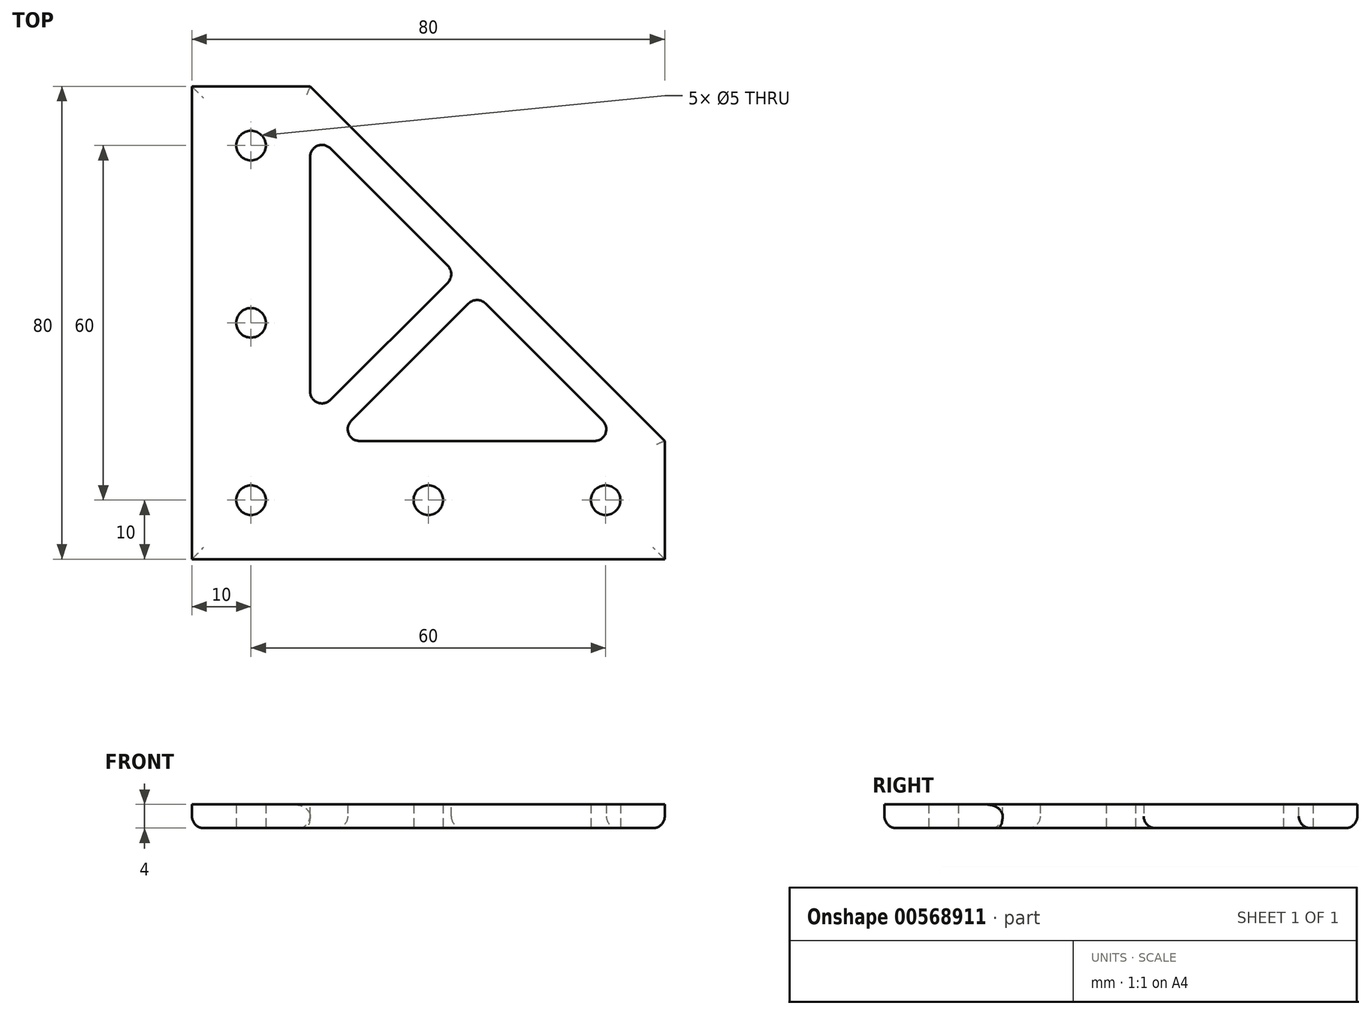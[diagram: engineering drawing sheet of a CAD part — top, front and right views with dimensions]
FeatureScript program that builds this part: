
annotation { "Feature Type Name" : "Feature", "Feature Type Description" : "" }
export const myFeature = defineFeature(function(context is Context, id is Id, definition is map)
    precondition{}
    {
        {
            var Q0;
            Q0=qCreatedBy(makeId("Top.planeOp"),FACE);
            var sketch = newSketch(context, id + "F0", { "sketchPlane" : qUnion([Q0])});
            skLineSegment(sketch, "E0", {"start": v(0, 0) * mm, "end": v(0, 80) * mm});
            skLineSegment(sketch, "E1", {"start": v(0, 80) * mm, "end": v(20, 80) * mm});
            skLineSegment(sketch, "E2", {"start": v(20, 80) * mm, "end": v(80, 20) * mm});
            skLineSegment(sketch, "E3", {"start": v(80, 20) * mm, "end": v(80, 0) * mm});
            skLineSegment(sketch, "E4", {"start": v(80, 0) * mm, "end": v(0, 0) * mm});
            skLineSegment(sketch, "E5", {"start": v(10, 80) * mm, "end": v(10, 0) * mm, "construction": true});
            skLineSegment(sketch, "E6", {"start": v(80, 10) * mm, "end": v(0, 10) * mm, "construction": true});
            skCircle(sketch, "E7", {"center": v(10, 70) * mm, "radius": 2.5 * mm});
            skCircle(sketch, "E8", {"center": v(10, 40) * mm, "radius": 2.5 * mm});
            skCircle(sketch, "E9", {"center": v(40, 10) * mm, "radius": 2.5 * mm});
            skCircle(sketch, "E10", {"center": v(70, 10) * mm, "radius": 2.5 * mm});
            skCircle(sketch, "E11", {"center": v(10, 10) * mm, "radius": 2.5 * mm});
            skSolve(sketch);
        }
        {
            var Q0;
            Q0=makeQuery(id+"F0.imprint","IMPRINT",FACE,{"disambiguationData":[TD([[makeQuery(id+"F0.imprint","IMPRINT",EDGE,{"derivedFrom":sQuery(id+"F0.wireOp",EDGE,"E0")}),-1.0]])]});
            extrude(context, id + "F1", {"entities" : qUnion([Q0]), "depth" : 4 * mm, "offsetDistance" : 25 * mm});
        }
        {
            var Q0;
            Q0=makeQuery(id+"F1.opExtrude","CAP_FACE",FACE,{"disambiguationData":[OSD([sQuery(id+"F0.wireOp",EDGE,"E0"),sQuery(id+"F0.wireOp",EDGE,"E1"),sQuery(id+"F0.wireOp",EDGE,"E2"),sQuery(id+"F0.wireOp",EDGE,"E3"),sQuery(id+"F0.wireOp",EDGE,"E4"),sQuery(id+"F0.wireOp",EDGE,"E7"),sQuery(id+"F0.wireOp",EDGE,"E8"),sQuery(id+"F0.wireOp",EDGE,"E9"),sQuery(id+"F0.wireOp",EDGE,"E10")])],"isStart":false});
            var sketch = newSketch(context, id + "F2", { "sketchPlane" : qUnion([Q0])});
            skLineSegment(sketch, "E12.0", {"start": v(20, 80) * mm, "end": v(80, 20) * mm, "construction": true});
            skLineSegment(sketch, "E13", {"start": v(20, 72.93) * mm, "end": v(20, 23.54) * mm});
            skLineSegment(sketch, "E14", {"start": v(72.93, 20) * mm, "end": v(23.54, 20) * mm});
            skPoint(sketch, "E15.orphan", {"position": v(20, 0) * mm});
            skLineSegment(sketch, "E16.0", {"start": v(20, 72.93) * mm, "end": v(44.7, 48.23) * mm});
            skLineSegment(sketch, "E17", {"start": v(20, 20) * mm, "end": v(46.46, 46.46) * mm, "construction": true});
            skLineSegment(sketch, "E18.0", {"start": v(20, 23.54) * mm, "end": v(44.7, 48.23) * mm});
            skLineSegment(sketch, "E19.0", {"start": v(23.54, 20) * mm, "end": v(48.23, 44.7) * mm});
            skLineSegment(sketch, "E20.trimOffspring", {"start": v(48.23, 44.7) * mm, "end": v(72.93, 20) * mm});
            skSolve(sketch);
        }
        {
            var Q0;
            Q0 = qSketchRegion(id + "F2", true);
            extrude(context, id + "F3", {"entities" : qUnion([Q0]), "operationType" : NewBodyOperationType.REMOVE, "oppositeDirection" : true, "depth" : 25 * mm, "offsetDistance" : 25 * mm});
        }
        {
            var Q0;
            Q0=makeQuery(id+"F1.opExtrude","CAP_EDGE",EDGE,{"disambiguationData":[OSD([sQuery(id+"F0.wireOp",EDGE,"E3")])],"isStart":true});
            var Q1;
            Q1=makeQuery(id+"F1.opExtrude","CAP_EDGE",EDGE,{"disambiguationData":[OSD([sQuery(id+"F0.wireOp",EDGE,"E2")])],"isStart":true});
            var Q2;
            Q2=makeQuery(id+"F1.opExtrude","CAP_EDGE",EDGE,{"disambiguationData":[OSD([sQuery(id+"F0.wireOp",EDGE,"E1")])],"isStart":true});
            var Q3;
            Q3=makeQuery(id+"F1.opExtrude","CAP_EDGE",EDGE,{"disambiguationData":[OSD([sQuery(id+"F0.wireOp",EDGE,"E0")])],"isStart":true});
            var Q4;
            Q4=makeQuery(id+"F1.opExtrude","CAP_EDGE",EDGE,{"disambiguationData":[OSD([sQuery(id+"F0.wireOp",EDGE,"E4")])],"isStart":true});
            var Q5;
            Q5=makeQuery(id+"F3.boolean.opBoolean","COPY",EDGE,{"derivedFrom":makeQuery(id+"F3.opExtrude","SWEPT_EDGE",EDGE,{"disambiguationData":[OSD([sQuery(id+"F2.wireOp",EDGE,"E14"),sQuery(id+"F2.wireOp",EDGE,"E20.trimOffspring")])]})});
            var Q6;
            Q6=makeQuery(id+"F3.boolean.opBoolean","COPY",EDGE,{"derivedFrom":makeQuery(id+"F3.opExtrude","SWEPT_EDGE",EDGE,{"disambiguationData":[OSD([sQuery(id+"F2.wireOp",EDGE,"E19.0"),sQuery(id+"F2.wireOp",EDGE,"E20.trimOffspring")])]})});
            var Q7;
            Q7=makeQuery(id+"F3.boolean.opBoolean","COPY",EDGE,{"derivedFrom":makeQuery(id+"F3.opExtrude","SWEPT_EDGE",EDGE,{"disambiguationData":[OSD([sQuery(id+"F2.wireOp",EDGE,"E14"),sQuery(id+"F2.wireOp",EDGE,"E19.0")])]})});
            var Q8;
            Q8=makeQuery(id+"F3.boolean.opBoolean","COPY",EDGE,{"derivedFrom":makeQuery(id+"F3.opExtrude","SWEPT_EDGE",EDGE,{"disambiguationData":[OSD([sQuery(id+"F2.wireOp",EDGE,"E16.0"),sQuery(id+"F2.wireOp",EDGE,"E18.0")])]})});
            var Q9;
            Q9=makeQuery(id+"F3.boolean.opBoolean","COPY",EDGE,{"derivedFrom":makeQuery(id+"F3.opExtrude","SWEPT_EDGE",EDGE,{"disambiguationData":[OSD([sQuery(id+"F2.wireOp",EDGE,"E13"),sQuery(id+"F2.wireOp",EDGE,"E18.0")])]})});
            var Q10;
            Q10=makeQuery(id+"F3.boolean.opBoolean","COPY",EDGE,{"derivedFrom":makeQuery(id+"F3.opExtrude","SWEPT_EDGE",EDGE,{"disambiguationData":[OSD([sQuery(id+"F2.wireOp",EDGE,"E13"),sQuery(id+"F2.wireOp",EDGE,"E16.0")])]})});
            fillet(context, id + "F4", {"entities" : qUnion([Q0, Q1, Q2, Q3, Q4, Q5, Q6, Q7, Q8, Q9, Q10]), "radius" : 2 * mm, "tangentPropagation" : true, "allowEdgeOverflow" : false});
        }
        {
            var Q0;
            Q0=makeQuery(id+"F3.boolean.opBoolean","INTERSECT",EDGE,{"derivedFrom":[makeQuery(id+"F1.opExtrude","CAP_FACE",FACE,{"disambiguationData":[OSD([sQuery(id+"F0.wireOp",EDGE,"E0"),sQuery(id+"F0.wireOp",EDGE,"E1"),sQuery(id+"F0.wireOp",EDGE,"E2"),sQuery(id+"F0.wireOp",EDGE,"E3"),sQuery(id+"F0.wireOp",EDGE,"E4"),sQuery(id+"F0.wireOp",EDGE,"E7"),sQuery(id+"F0.wireOp",EDGE,"E8"),sQuery(id+"F0.wireOp",EDGE,"E9"),sQuery(id+"F0.wireOp",EDGE,"E10")])],"isStart":true}),makeQuery(id+"F3.opExtrude","SWEPT_FACE",FACE,{"disambiguationData":[OSD([sQuery(id+"F2.wireOp",EDGE,"E14")])]})]});
            var Q1;
            Q1=makeQuery(id+"F3.boolean.opBoolean","INTERSECT",EDGE,{"derivedFrom":[makeQuery(id+"F1.opExtrude","CAP_FACE",FACE,{"disambiguationData":[OSD([sQuery(id+"F0.wireOp",EDGE,"E0"),sQuery(id+"F0.wireOp",EDGE,"E1"),sQuery(id+"F0.wireOp",EDGE,"E2"),sQuery(id+"F0.wireOp",EDGE,"E3"),sQuery(id+"F0.wireOp",EDGE,"E4"),sQuery(id+"F0.wireOp",EDGE,"E7"),sQuery(id+"F0.wireOp",EDGE,"E8"),sQuery(id+"F0.wireOp",EDGE,"E9"),sQuery(id+"F0.wireOp",EDGE,"E10")])],"isStart":true}),makeQuery(id+"F3.opExtrude","SWEPT_FACE",FACE,{"disambiguationData":[OSD([sQuery(id+"F2.wireOp",EDGE,"E13")])]})]});
            var Q2;
            Q2=makeQuery(id+"F1.opExtrude","CAP_EDGE",EDGE,{"disambiguationData":[OSD([sQuery(id+"F0.wireOp",EDGE,"E2")])],"isStart":false});
            var Q3;
            Q3=makeQuery(id+"F3.boolean.opBoolean","COPY",EDGE,{"derivedFrom":makeQuery(id+"F3.opExtrude","CAP_EDGE",EDGE,{"disambiguationData":[OSD([sQuery(id+"F2.wireOp",EDGE,"E18.0")])],"isStart":true})});
            var Q4;
            Q4=makeQuery(id+"F3.boolean.opBoolean","COPY",EDGE,{"derivedFrom":makeQuery(id+"F3.opExtrude","CAP_EDGE",EDGE,{"disambiguationData":[OSD([sQuery(id+"F2.wireOp",EDGE,"E20.trimOffspring")])],"isStart":true})});
            fillet(context, id + "F5", {"entities" : qUnion([Q0, Q1, Q2, Q3, Q4]), "radius" : 2 * mm, "tangentPropagation" : true, "allowEdgeOverflow" : false});
        }
    });
